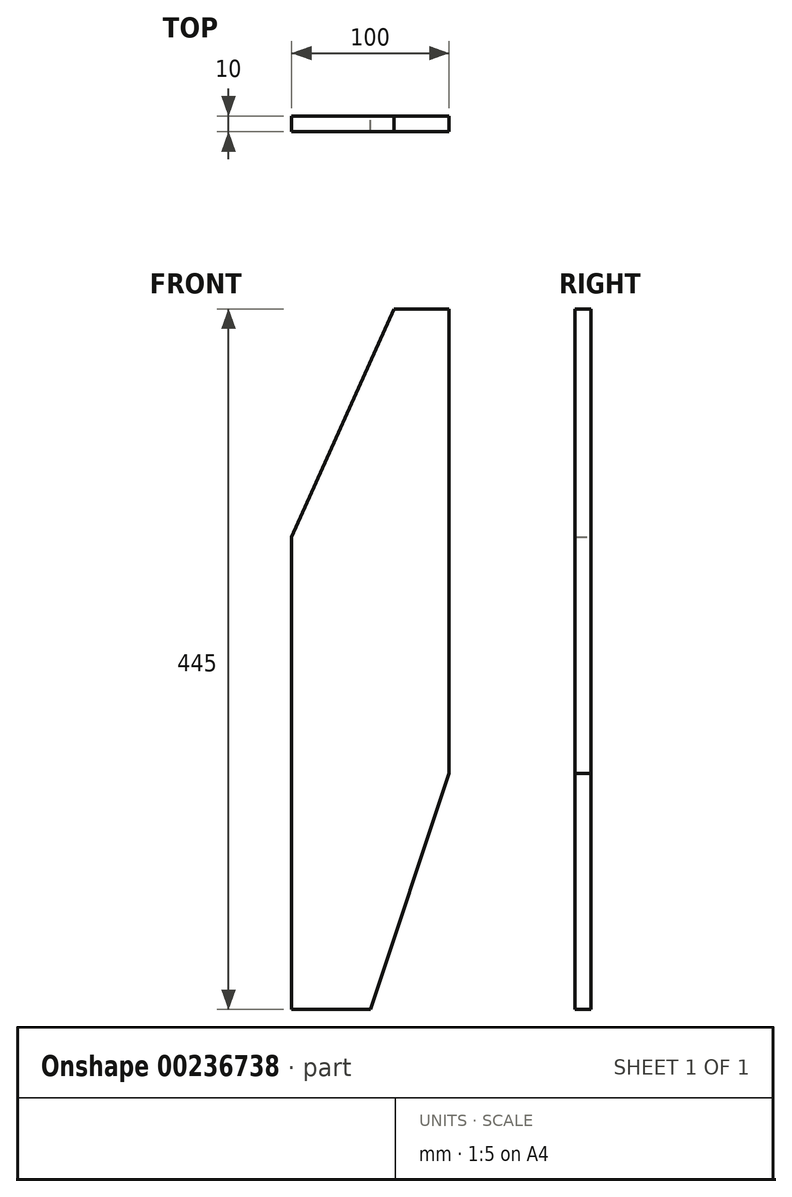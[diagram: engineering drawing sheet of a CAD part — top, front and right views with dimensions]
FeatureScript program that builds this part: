
annotation { "Feature Type Name" : "Feature", "Feature Type Description" : "" }
export const myFeature = defineFeature(function(context is Context, id is Id, definition is map)
    precondition{}
    {
        {
            var Q0;
            Q0=qCreatedBy(makeId("Front.planeOp"), FACE);
            var sketch = newSketch(context, id + "F0", { "sketchPlane" : qUnion([Q0])});
            skLineSegment(sketch, "E0.bottom", {"start": v(0, 0) * mm, "end": v(50, 0) * mm});
            skLineSegment(sketch, "E0.left", {"start": v(0, 0) * mm, "end": v(0, 300) * mm});
            skLineSegment(sketch, "E1", {"start": v(100, 150) * mm, "end": v(50, 0) * mm});
            skPoint(sketch, "E2.orphan", {"position": v(100, 0) * mm});
            skLineSegment(sketch, "E3", {"start": v(0, 300) * mm, "end": v(65.17, 445) * mm});
            skLineSegment(sketch, "E4", {"start": v(65.17, 445) * mm, "end": v(100, 445) * mm});
            skLineSegment(sketch, "E5", {"start": v(100, 445) * mm, "end": v(100, 150) * mm});
            skSolve(sketch);
        }
        {
            var Q0;
            Q0 = qSketchRegion(id + "F0", true);
            extrude(context, id + "F1", {"entities" : qUnion([Q0]), "depth" : 10 * mm, "offsetDistance" : 25 * mm});
        }
    });
